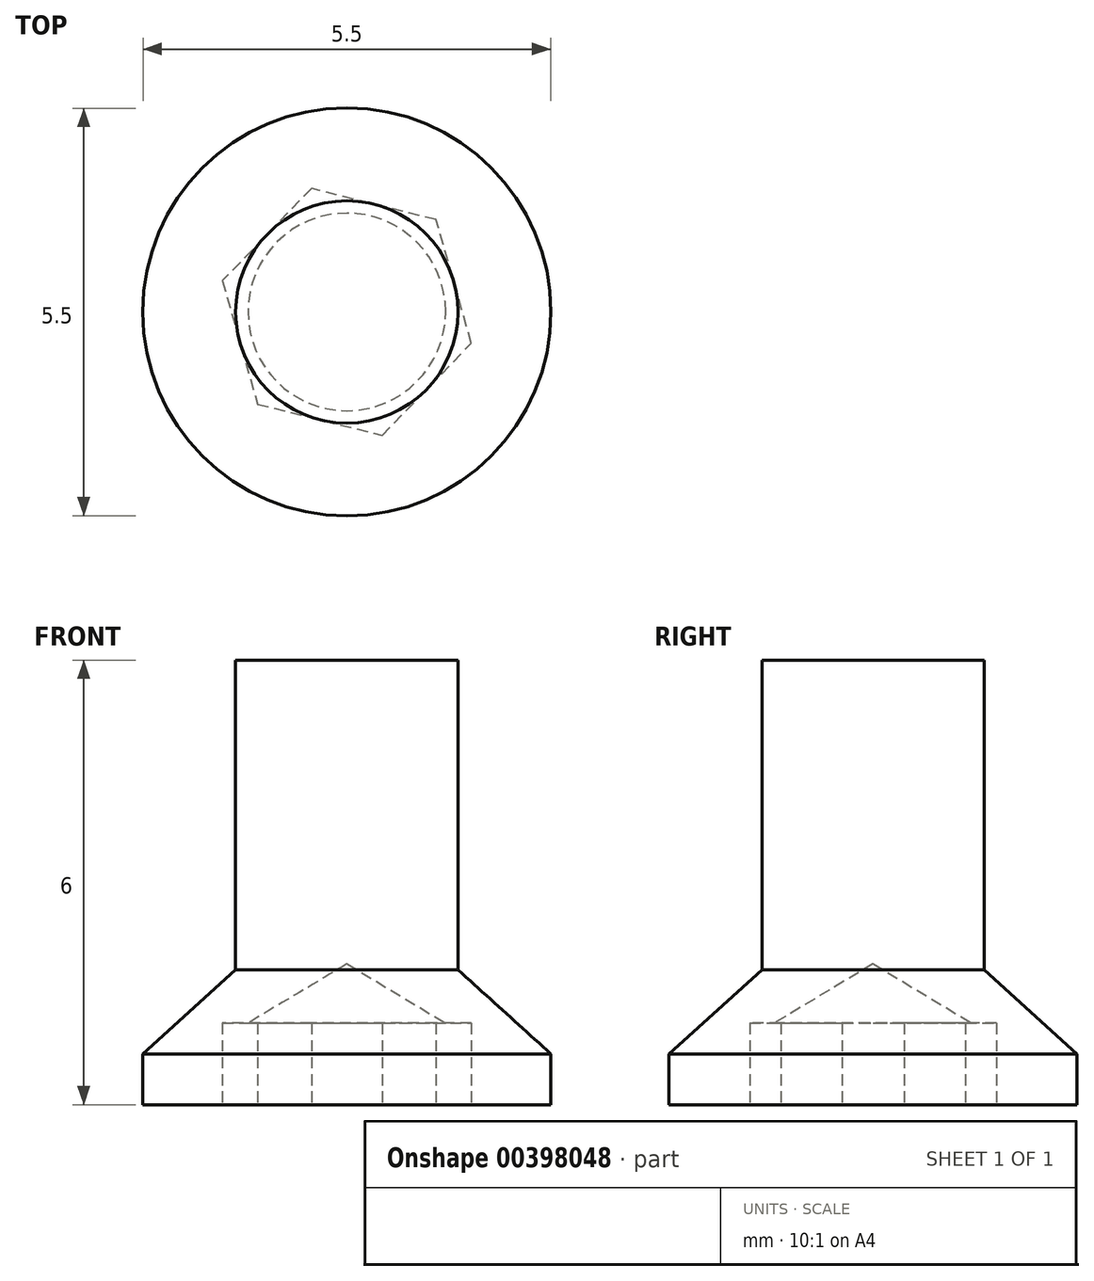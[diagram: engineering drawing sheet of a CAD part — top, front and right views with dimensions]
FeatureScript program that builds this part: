
annotation { "Feature Type Name" : "Feature", "Feature Type Description" : "" }
export const myFeature = defineFeature(function(context is Context, id is Id, definition is map)
    precondition{}
    {
        {
            var Q0;
            Q0=qCreatedBy(makeId("Front.planeOp"),FACE);
            var sketch = newSketch(context, id + "F0", { "sketchPlane" : qUnion([Q0])});
            skLineSegment(sketch, "E0", {"start": v(0, 6) * mm, "end": v(1.5, 6) * mm});
            skLineSegment(sketch, "E1", {"start": v(1.5, 6) * mm, "end": v(1.5, 1.82) * mm});
            skLineSegment(sketch, "E2", {"start": v(1.5, 1.82) * mm, "end": v(2.75, 0.69) * mm});
            skLineSegment(sketch, "E3", {"start": v(2.75, 0.69) * mm, "end": v(2.75, 0) * mm});
            skLineSegment(sketch, "E4", {"start": v(0, 6) * mm, "end": v(0, 0) * mm});
            skLineSegment(sketch, "E5", {"start": v(0, 0) * mm, "end": v(3.17, 0) * mm});
            skSolve(sketch);
        }
        {
            var Q0;
            Q0 = qSketchRegion(id + "F0", true);
            var Q1;
            Q1=sQuery(id+"F0.wireOp",EDGE,"E4");
            revolve(context, id + "F1", {"entities" : qUnion([Q0]), "axis" : qUnion([Q1]), "revolveType" : RevolveType.FULL});
        }
        {
            var Q0;
            Q0=makeQuery(id+"F1.opRevolve","SWEPT_FACE",FACE,{"disambiguationData":[OSD([sQuery(id+"F0.wireOp",EDGE,"E5")])]});
            var sketch = newSketch(context, id + "F2", { "sketchPlane" : qUnion([Q0])});
            skPoint(sketch, "E6", {"position": v(0, 0) * mm});
            skSolve(sketch);
        }
        {
            var Q0;
            Q0=sQuery(id+"F2.wireOp",VERTEX,"E6");
            var Q1;
            Q1=makeQuery(id+"F1.opRevolve","SWEPT_BODY",BODY,{"disambiguationData":[OSD([sQuery(id+"F0.wireOp",EDGE,"E0"),sQuery(id+"F0.wireOp",EDGE,"E1"),sQuery(id+"F0.wireOp",EDGE,"E2"),sQuery(id+"F0.wireOp",EDGE,"E3"),sQuery(id+"F0.wireOp",EDGE,"E4"),sQuery(id+"F0.wireOp",EDGE,"E5")])]});
            hole(context, id + "F3", {"style" : HoleStyle.SIMPLE, "endStyle" : HoleEndStyle.BLIND, "holeDiameter" : 3 * mm, "holeDepth" : 1 * mm, "isTappedThrough" : true, "tappedDepth" : 12 * mm, "tapClearance" : 3, "startFromSketch" : true, "locations" : qUnion([Q0]), "scope" : qUnion([Q1])});
        }
        {
            var Q0;
            Q0=makeQuery(id+"F1.opRevolve","SWEPT_FACE",FACE,{"disambiguationData":[OSD([sQuery(id+"F0.wireOp",EDGE,"E5")])]});
            var sketch = newSketch(context, id + "F4", { "sketchPlane" : qUnion([Q0])});
            skCircle(sketch, "E7.0", {"center": v(0, 0) * mm, "radius": 1.5 * mm});
            skCircle(sketch, "E8.cCircle", {"center": v(0, 0) * mm, "radius": 1.5 * mm, "construction": true});
            skLineSegment(sketch, "E8.0", {"start": v(1.2, -1.25) * mm, "end": v(-0.48, -1.67) * mm});
            skLineSegment(sketch, "E8.1", {"start": v(-0.48, -1.67) * mm, "end": v(-1.68, -0.42) * mm});
            skLineSegment(sketch, "E8.2", {"start": v(-1.68, -0.42) * mm, "end": v(-1.2, 1.25) * mm});
            skLineSegment(sketch, "E8.3", {"start": v(-1.2, 1.25) * mm, "end": v(0.48, 1.67) * mm});
            skLineSegment(sketch, "E8.4", {"start": v(0.48, 1.67) * mm, "end": v(1.68, 0.42) * mm});
            skLineSegment(sketch, "E8.5", {"start": v(1.68, 0.42) * mm, "end": v(1.2, -1.25) * mm});
            skPoint(sketch, "E8.0.midPoint", {"position": v(0.36, -1.46) * mm});
            skSolve(sketch);
        }
        {
            var Q0;
            Q0 = qSketchRegion(id + "F4", true);
            extrude(context, id + "F5", {"entities" : qUnion([Q0]), "operationType" : NewBodyOperationType.REMOVE, "oppositeDirection" : true, "depth" : 1.1 * mm});
        }
    });
